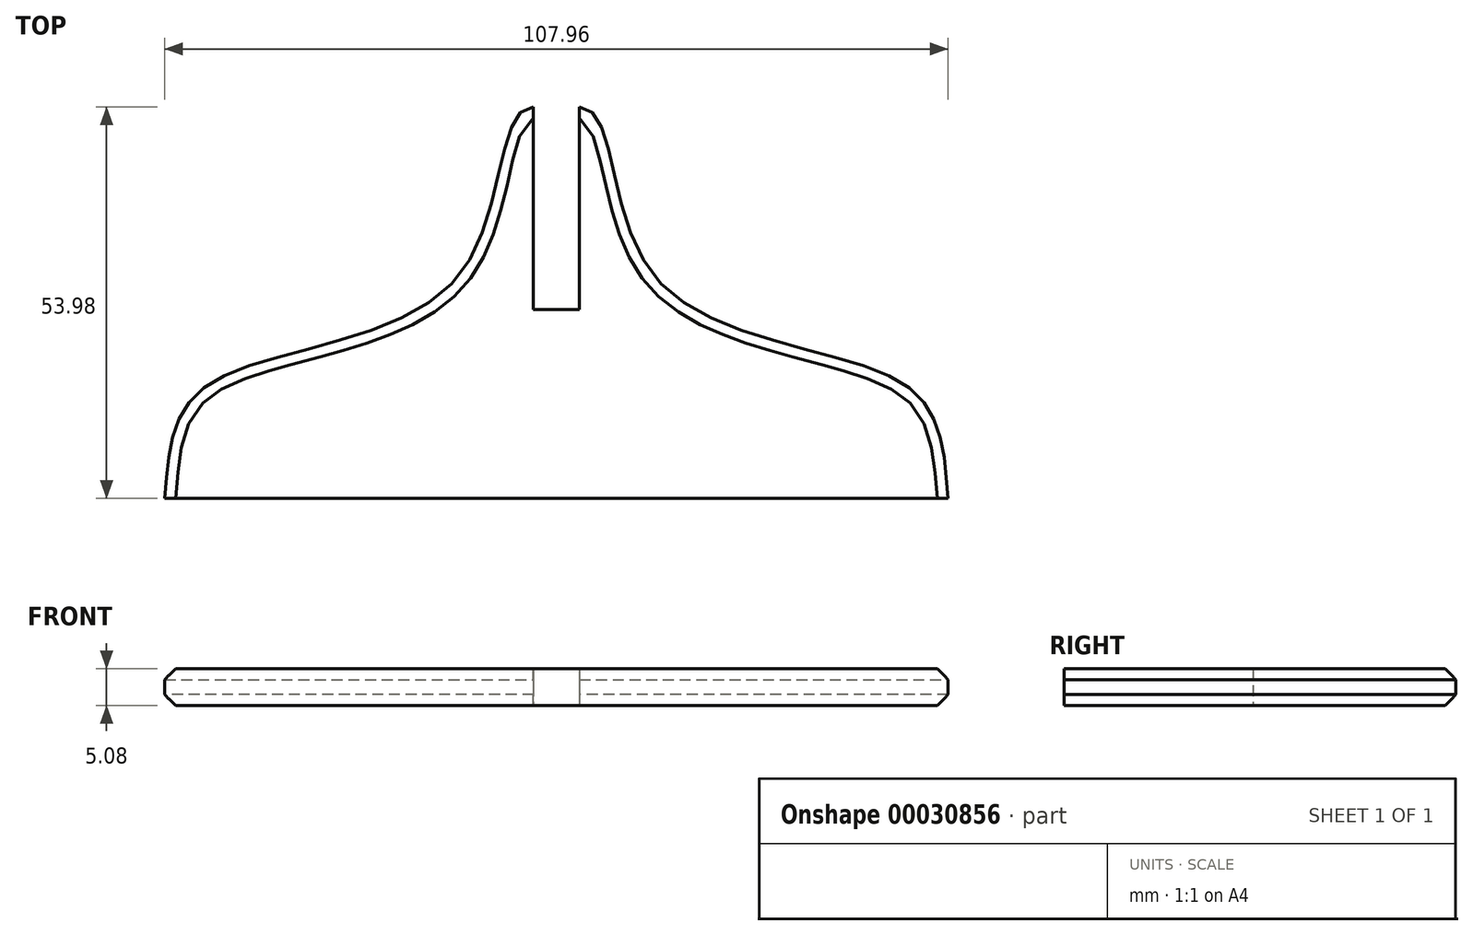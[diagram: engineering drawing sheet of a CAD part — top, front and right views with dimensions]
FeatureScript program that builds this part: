
annotation { "Feature Type Name" : "Feature", "Feature Type Description" : "" }
export const myFeature = defineFeature(function(context is Context, id is Id, definition is map)
    precondition{}
    {
        {
            var Q0;
            Q0=qCreatedBy(makeId("Top.planeOp"),FACE);
            var sketch = newSketch(context, id + "F0", { "sketchPlane" : qUnion([Q0])});
            skLineSegment(sketch, "E0", {"start": v(-53.98, -13.94) * mm, "end": v(53.98, -13.94) * mm});
            skPoint(sketch, "E1", {"position": v(0, -13.94) * mm});
            skLineSegment(sketch, "E2", {"start": v(0, -13.94) * mm, "end": v(0, 40.04) * mm, "construction": true});
            skLineSegment(sketch, "E3", {"start": v(-3.18, 40.04) * mm, "end": v(3.18, 40.04) * mm, "construction": true});
            skPoint(sketch, "E4", {"position": v(0, 40.04) * mm});
            skFitSpline(sketch, "E5", {"points": [v(-3.18, 40.04) * mm, v(-13.2, 17.05) * mm, v(-48.33, 1.5) * mm, v(-53.97, -13.94) * mm], "startDerivative": vector(-47.95, -1.4) * mm, "endDerivative": vector(-5.9, -64.9) * mm});
            skFitSpline(sketch, "E6.MirrorCS", {"points": [v(3.18, 40.04) * mm, v(13.2, 17.05) * mm, v(48.33, 1.5) * mm, v(53.97, -13.94) * mm], "startDerivative": vector(47.95, -1.4) * mm, "endDerivative": vector(5.9, -64.9) * mm});
            skLineSegment(sketch, "E7", {"start": v(-3.17, 40.04) * mm, "end": v(-3.17, 12.1) * mm});
            skLineSegment(sketch, "E8", {"start": v(3.17, 40.04) * mm, "end": v(3.17, 12.1) * mm});
            skLineSegment(sketch, "E9", {"start": v(3.17, 12.1) * mm, "end": v(-3.17, 12.1) * mm});
            skSolve(sketch);
        }
        {
            var Q0;
            Q0 = qSketchRegion(id + "F0", true);
            extrude(context, id + "F1", {"entities" : qUnion([Q0]), "depth" : 5.08 * mm});
        }
        {
            var Q0;
            Q0=makeQuery(id+"F1.opExtrude","CAP_EDGE",EDGE,{"disambiguationData":[OSD([sQuery(id+"F0.wireOp",EDGE,"E5")])],"isStart":false});
            var Q1;
            Q1=makeQuery(id+"F1.opExtrude","CAP_EDGE",EDGE,{"disambiguationData":[OSD([sQuery(id+"F0.wireOp",EDGE,"E6.MirrorCS")])],"isStart":false});
            var Q2;
            Q2=makeQuery(id+"F1.opExtrude","CAP_EDGE",EDGE,{"disambiguationData":[OSD([sQuery(id+"F0.wireOp",EDGE,"E6.MirrorCS")])],"isStart":true});
            var Q3;
            Q3=makeQuery(id+"F1.opExtrude","CAP_EDGE",EDGE,{"disambiguationData":[OSD([sQuery(id+"F0.wireOp",EDGE,"E5")])],"isStart":true});
            chamfer(context, id + "F2", {"entities" : qUnion([Q0, Q1, Q2, Q3]), "width" : 1.5 * mm});
        }
    });
